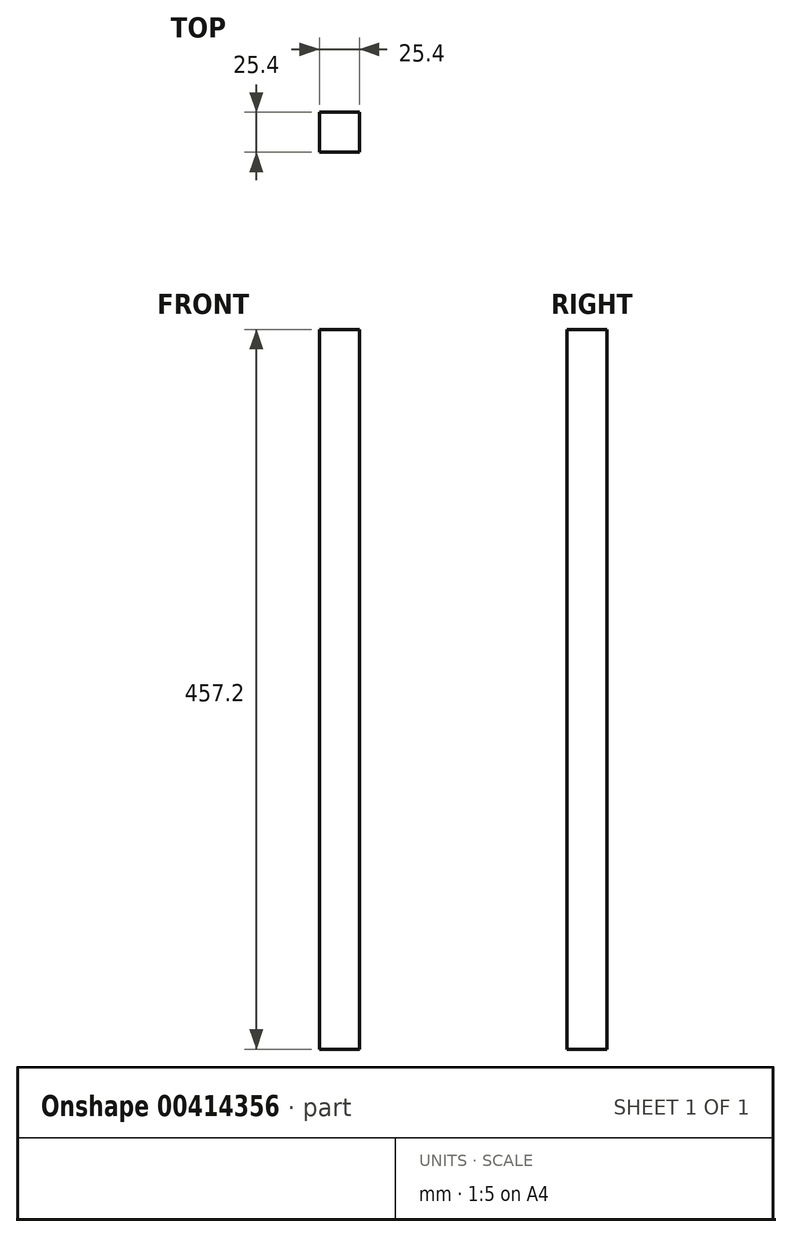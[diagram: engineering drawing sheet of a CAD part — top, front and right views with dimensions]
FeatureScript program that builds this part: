
annotation { "Feature Type Name" : "Feature", "Feature Type Description" : "" }
export const myFeature = defineFeature(function(context is Context, id is Id, definition is map)
    precondition{}
    {
        {
            var Q0;
            Q0=qCreatedBy(makeId("Top.planeOp"),FACE);
            var sketch = newSketch(context, id + "F0", { "sketchPlane" : qUnion([Q0])});
            skLineSegment(sketch, "E0.bottom", {"start": v(12.7, -12.7) * mm, "end": v(-12.7, -12.7) * mm});
            skLineSegment(sketch, "E0.top", {"start": v(12.7, 12.7) * mm, "end": v(-12.7, 12.7) * mm});
            skLineSegment(sketch, "E0.left", {"start": v(12.7, -12.7) * mm, "end": v(12.7, 12.7) * mm});
            skLineSegment(sketch, "E0.right", {"start": v(-12.7, -12.7) * mm, "end": v(-12.7, 12.7) * mm});
            skPoint(sketch, "E0.middle", {"position": v(0, 0) * mm});
            skSolve(sketch);
        }
        {
            var Q0;
            Q0 = qSketchRegion(id + "F0", true);
            extrude(context, id + "F1", {"entities" : qUnion([Q0]), "depth" : 457.2 * mm});
        }
    });
